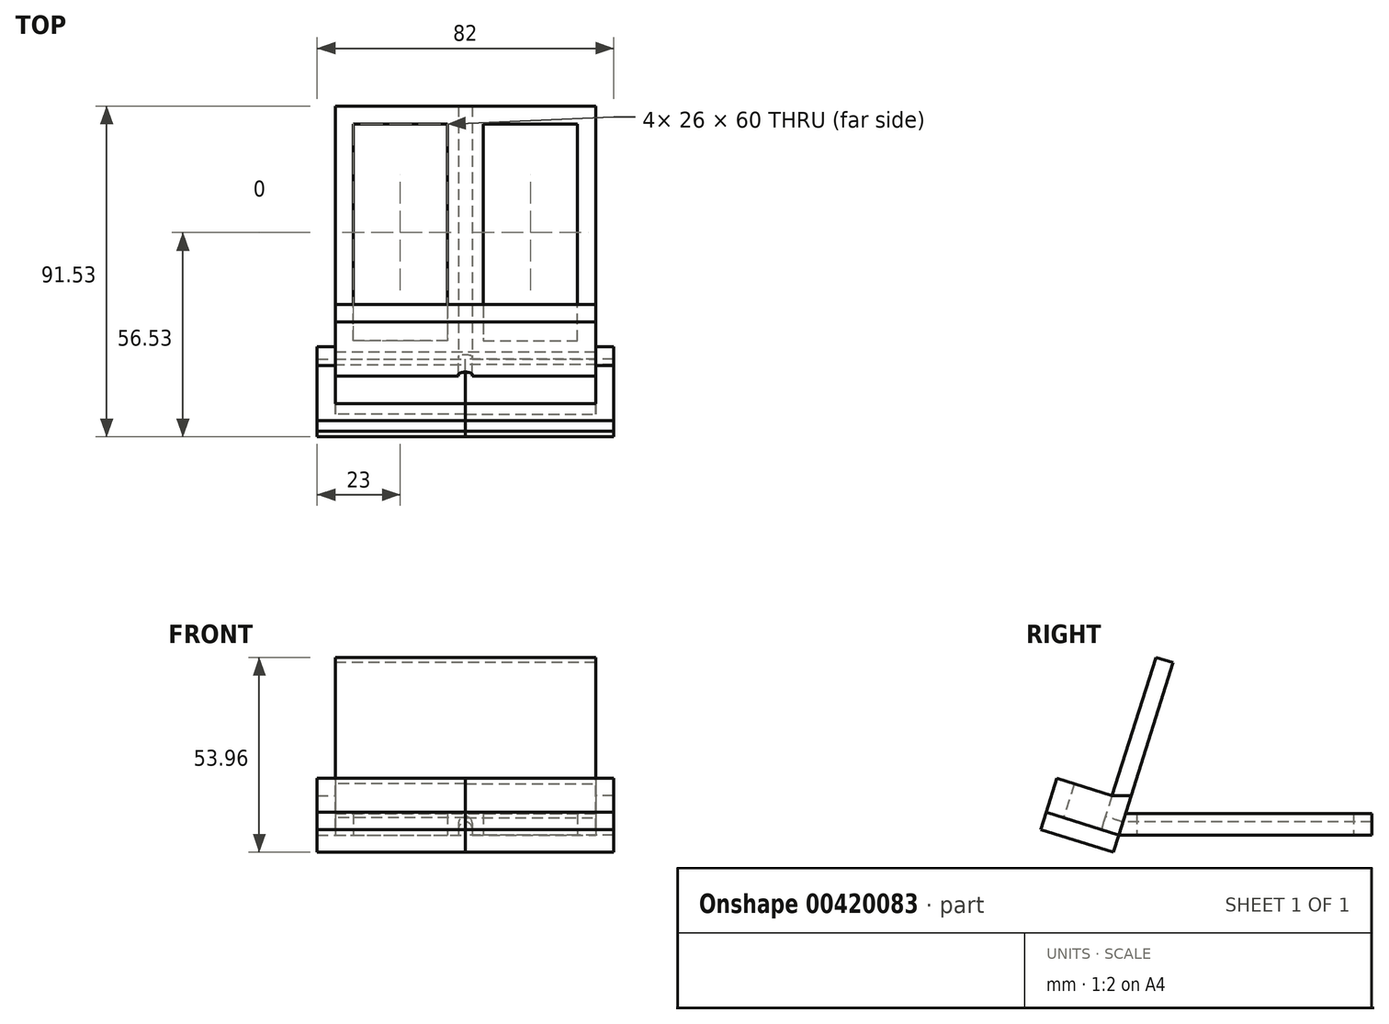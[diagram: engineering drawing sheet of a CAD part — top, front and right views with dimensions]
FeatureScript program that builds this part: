
annotation { "Feature Type Name" : "Feature", "Feature Type Description" : "" }
export const myFeature = defineFeature(function(context is Context, id is Id, definition is map)
    precondition{}
    {
        {
            var Q0;
            Q0=qCreatedBy(makeId("Top.planeOp"),FACE);
            var sketch = newSketch(context, id + "F0", { "sketchPlane" : qUnion([Q0])});
            skLineSegment(sketch, "E0", {"start": v(0, 0) * mm, "end": v(36, 0) * mm});
            skLineSegment(sketch, "E1", {"start": v(36, 0) * mm, "end": v(36, 70) * mm});
            skLineSegment(sketch, "E2", {"start": v(36, 70) * mm, "end": v(0, 70) * mm});
            skLineSegment(sketch, "E3", {"start": v(5, 65) * mm, "end": v(5, 5) * mm});
            skLineSegment(sketch, "E4", {"start": v(5, 5) * mm, "end": v(31, 5) * mm});
            skLineSegment(sketch, "E5", {"start": v(31, 5) * mm, "end": v(31, 65) * mm});
            skLineSegment(sketch, "E6", {"start": v(31, 65) * mm, "end": v(5, 65) * mm});
            skLineSegment(sketch, "E7.MirrorCS", {"start": v(-36, 70) * mm, "end": v(0, 70) * mm});
            skLineSegment(sketch, "E8.MirrorCS", {"start": v(-5, 65) * mm, "end": v(-5, 5) * mm});
            skLineSegment(sketch, "E9.MirrorCS", {"start": v(0, 0) * mm, "end": v(-36, 0) * mm});
            skLineSegment(sketch, "E10.MirrorCS", {"start": v(-36, 0) * mm, "end": v(-36, 70) * mm});
            skLineSegment(sketch, "E11.MirrorCS", {"start": v(-31, 5) * mm, "end": v(-31, 65) * mm});
            skLineSegment(sketch, "E12.MirrorCS", {"start": v(-31, 65) * mm, "end": v(-5, 65) * mm});
            skLineSegment(sketch, "E13.MirrorCS", {"start": v(-5, 5) * mm, "end": v(-31, 5) * mm});
            skSolve(sketch);
        }
        {
            var Q0;
            Q0=makeQuery(id+"F0.imprint","IMPRINT",FACE,{"disambiguationData":[TD([[makeQuery(id+"F0.imprint","IMPRINT",EDGE,{"derivedFrom":sQuery(id+"F0.wireOp",EDGE,"E0")}),1.0]])]});
            extrude(context, id + "F1", {"entities" : qUnion([Q0]), "depth" : 6 * mm});
        }
        {
            var Q0;
            Q0=makeQuery(id+"F1.opExtrude","SWEPT_FACE",FACE,{"disambiguationData":[OSD([sQuery(id+"F0.wireOp",EDGE,"E0"),sQuery(id+"F0.wireOp",EDGE,"E9.MirrorCS")])]});
            var sketch = newSketch(context, id + "F2", { "sketchPlane" : qUnion([Q0])});
            skArc(sketch, "E14", {"start": v(0, 3.65) * mm, "mid": v(-1.35, 3.1) * mm, "end": v(-1.9, 1.75) * mm});
            skLineSegment(sketch, "E15.MirrorCS", {"start": v(0, -0.15) * mm, "end": v(-1.9, -0.15) * mm});
            skLineSegment(sketch, "E16", {"start": v(-1.9, 1.75) * mm, "end": v(-1.9, -0.15) * mm});
            skPoint(sketch, "E17.orphan", {"position": v(-4.72, -0.15) * mm});
            skPoint(sketch, "E18.end.orphan", {"position": v(4.72, -0.15) * mm});
            skPoint(sketch, "E18.start.orphan", {"position": v(0, -0.15) * mm});
            skPoint(sketch, "E19.orphan", {"position": v(0, 4.82) * mm});
            skLineSegment(sketch, "E20.MirrorCS", {"start": v(1.9, 1.75) * mm, "end": v(1.9, -0.15) * mm});
            skLineSegment(sketch, "E21.MirrorCS", {"start": v(0, -0.15) * mm, "end": v(1.9, -0.15) * mm});
            skArc(sketch, "E22.MirrorCS", {"start": v(0, 3.65) * mm, "mid": v(1.35, 3.1) * mm, "end": v(1.9, 1.75) * mm});
            skSolve(sketch);
        }
        {
            var Q0;
            {var subQ5=sQuery(id+"F2.wireOp",EDGE,"E14");Q0=makeQuery(id+"F2.imprint","IMPRINT",FACE,{"disambiguationData":[TD([[makeQuery(id+"F2.imprint","IMPRINT",EDGE,{"derivedFrom":subQ5}),1.0]])]});}
            extrude(context, id + "F3", {"entities" : qUnion([Q0]), "operationType" : NewBodyOperationType.REMOVE, "oppositeDirection" : true, "depth" : 100 * mm});
        }
        {
            var Q0;
            Q0=makeQuery(id+"F1.opExtrude","SWEPT_FACE",FACE,{"disambiguationData":[OSD([sQuery(id+"F0.wireOp",EDGE,"E1")])]});
            var sketch = newSketch(context, id + "F4", { "sketchPlane" : qUnion([Q0])});
            skLineSegment(sketch, "E23", {"start": v(0, 0) * mm, "end": v(1.9, 6) * mm});
            skLineSegment(sketch, "E24", {"start": v(1.9, 6) * mm, "end": v(0, 6) * mm});
            skLineSegment(sketch, "E25", {"start": v(0, 6) * mm, "end": v(0, 0) * mm});
            skSolve(sketch);
        }
        {
            var Q0;
            Q0=makeQuery(id+"F4.imprint","IMPRINT",FACE,{"disambiguationData":[TD([[makeQuery(id+"F4.imprint","IMPRINT",EDGE,{"derivedFrom":sQuery(id+"F4.wireOp",EDGE,"E23")}),1.0]])]});
            extrude(context, id + "F5", {"entities" : qUnion([Q0]), "operationType" : NewBodyOperationType.REMOVE, "oppositeDirection" : true, "depth" : 75 * mm});
        }
        {
            var Q0;
            Q0=makeQuery(id+"F5.boolean.opBoolean","COPY",FACE,{"derivedFrom":makeQuery(id+"F5.opExtrude","SWEPT_FACE",FACE,{"disambiguationData":[OSD([sQuery(id+"F4.wireOp",EDGE,"E23")])]})});
            var sketch = newSketch(context, id + "F6", { "sketchPlane" : qUnion([Q0])});
            skLineSegment(sketch, "E26", {"start": v(-36, 0) * mm, "end": v(-36, 50) * mm});
            skLineSegment(sketch, "E27", {"start": v(-36, 50) * mm, "end": v(36, 50) * mm});
            skLineSegment(sketch, "E28", {"start": v(36, 50) * mm, "end": v(36, 0) * mm});
            skSolve(sketch);
        }
        {
            var Q0;
            {var subQ2=sQuery(id+"F6.wireOp",EDGE,"E27");Q0=makeQuery(id+"F6.imprint","IMPRINT",FACE,{"disambiguationData":[TD([[makeQuery(id+"F6.imprint","IMPRINT",EDGE,{"derivedFrom":subQ2}),-1.0]])]});}
            var Q1;
            {var subQ0=sQuery(id+"F4.wireOp",EDGE,"E23");var subQ13=makeQuery(id+"F3.opExtrude","SWEPT_FACE",FACE,{"disambiguationData":[OSD([sQuery(id+"F2.wireOp",EDGE,"E16")])]});var subQ16=makeQuery(id+"F5.opExtrude","SWEPT_FACE",FACE,{"disambiguationData":[OSD([subQ0])]});Q1=makeQuery(id+"F6.imprint","IMPRINT",FACE,{"disambiguationData":[TD([[makeQuery(id+"F6.imprint","IMPRINT",EDGE,{"derivedFrom":makeQuery(id+"F5.boolean.opBoolean","INTERSECT",EDGE,{"derivedFrom":[makeQuery(id+"F3.boolean.opBoolean","COPY",FACE,{"derivedFrom":subQ13}),subQ16]})}),-1.0]])]});}
            extrude(context, id + "F7", {"entities" : qUnion([Q0, Q1]), "operationType" : NewBodyOperationType.ADD, "depth" : 5 * mm});
        }
        {
            var Q0;
            Q0=makeQuery(id+"F7.boolean.opBoolean","MERGE",FACE,{"derivedFrom":[makeQuery(id+"F1.opExtrude","SWEPT_FACE",FACE,{"disambiguationData":[OSD([sQuery(id+"F0.wireOp",EDGE,"E1")])]}),makeQuery(id+"F7.opExtrude","SWEPT_FACE",FACE,{"disambiguationData":[OSD([sQuery(id+"F6.wireOp",EDGE,"E28")])]})]});
            var sketch = newSketch(context, id + "F8", { "sketchPlane" : qUnion([Q0])});
            skLineSegment(sketch, "E29", {"start": v(-1.8, 10.89) * mm, "end": v(3.44, 10.89) * mm});
            skLineSegment(sketch, "E30", {"start": v(3.44, 10.89) * mm, "end": v(0, 0) * mm});
            skLineSegment(sketch, "E31", {"start": v(0, 0) * mm, "end": v(-4.77, 1.5) * mm});
            skLineSegment(sketch, "E32", {"start": v(-4.77, 1.5) * mm, "end": v(-1.8, 10.89) * mm});
            skSolve(sketch);
        }
        {
            var Q0;
            {var subQ4=sQuery(id+"F8.wireOp",EDGE,"E29");Q0=makeQuery(id+"F8.imprint","IMPRINT",FACE,{"disambiguationData":[TD([[makeQuery(id+"F8.imprint","IMPRINT",EDGE,{"derivedFrom":subQ4}),-1.0]])]});}
            extrude(context, id + "F9", {"entities" : qUnion([Q0]), "operationType" : NewBodyOperationType.ADD, "depth" : 5 * mm});
        }
        {
            var Q0;
            Q0=makeQuery(id+"F9.boolean.opBoolean","MERGE",FACE,{"derivedFrom":[makeQuery(id+"F7.opExtrude","CAP_FACE",FACE,{"disambiguationData":[OSD([sQuery(id+"F0.wireOp",EDGE,"E0"),sQuery(id+"F0.wireOp",EDGE,"E1"),sQuery(id+"F0.wireOp",EDGE,"E9.MirrorCS"),sQuery(id+"F2.wireOp",EDGE,"E14"),sQuery(id+"F2.wireOp",EDGE,"E16"),sQuery(id+"F2.wireOp",EDGE,"E20.MirrorCS"),sQuery(id+"F2.wireOp",EDGE,"E22.MirrorCS"),sQuery(id+"F4.wireOp",EDGE,"E23"),sQuery(id+"F4.wireOp",EDGE,"E25"),sQuery(id+"F6.wireOp",EDGE,"E26"),sQuery(id+"F6.wireOp",EDGE,"E27"),sQuery(id+"F6.wireOp",EDGE,"E28")])],"isStart":false}),makeQuery(id+"F9.opExtrude","SWEPT_FACE",FACE,{"disambiguationData":[OSD([sQuery(id+"F8.wireOp",EDGE,"E32")])]})]});
            var sketch = newSketch(context, id + "F10", { "sketchPlane" : qUnion([Q0])});
            skLineSegment(sketch, "E33", {"start": v(36, 9.84) * mm, "end": v(36, 0) * mm});
            skSolve(sketch);
        }
        {
            var Q0;
            {var subQ0=sQuery(id+"F10.wireOp",EDGE,"E33");Q0=makeQuery(id+"F10.imprint","IMPRINT",FACE,{"disambiguationData":[TD([[makeQuery(id+"F10.imprint","IMPRINT",EDGE,{"derivedFrom":subQ0}),1.0]])]});}
            extrude(context, id + "F11", {"entities" : qUnion([Q0]), "operationType" : NewBodyOperationType.ADD, "depth" : 16 * mm});
        }
        {
            var Q0;
            Q0=makeQuery(id+"F11.opExtrude","SWEPT_FACE",FACE,{"disambiguationData":[OSD([sQuery(id+"F10.wireOp",EDGE,"E33")])]});
            var sketch = newSketch(context, id + "F12", { "sketchPlane" : qUnion([Q0])});
            skLineSegment(sketch, "E34", {"start": v(17.07, 15.7) * mm, "end": v(12.3, 14.2) * mm});
            skPoint(sketch, "E35.endSnap0", {"position": v(12.4, 3.91) * mm});
            skPoint(sketch, "E35.end.orphan", {"position": v(15.54, 3.91) * mm});
            skLineSegment(sketch, "E36", {"start": v(12.3, 14.2) * mm, "end": v(15.26, 4.82) * mm});
            skSolve(sketch);
        }
        {
            var Q0;
            Q0=makeQuery(id+"F12.imprint","IMPRINT",FACE,{"disambiguationData":[TD([[makeQuery(id+"F12.imprint","IMPRINT",EDGE,{"derivedFrom":sQuery(id+"F12.wireOp",EDGE,"E34")}),1.0]])]});
            extrude(context, id + "F13", {"entities" : qUnion([Q0]), "operationType" : NewBodyOperationType.ADD, "depth" : 36 * mm});
        }
        {
            var Q0;
            Q0=makeQuery(id+"F1.opExtrude","SWEPT_BODY",BODY,{"disambiguationData":[OSD([sQuery(id+"F0.wireOp",EDGE,"E0"),sQuery(id+"F0.wireOp",EDGE,"E1"),sQuery(id+"F0.wireOp",EDGE,"E2"),sQuery(id+"F0.wireOp",EDGE,"E3"),sQuery(id+"F0.wireOp",EDGE,"E4"),sQuery(id+"F0.wireOp",EDGE,"E5"),sQuery(id+"F0.wireOp",EDGE,"E6"),sQuery(id+"F0.wireOp",EDGE,"E7.MirrorCS"),sQuery(id+"F0.wireOp",EDGE,"E8.MirrorCS"),sQuery(id+"F0.wireOp",EDGE,"E9.MirrorCS"),sQuery(id+"F0.wireOp",EDGE,"E10.MirrorCS"),sQuery(id+"F0.wireOp",EDGE,"E11.MirrorCS"),sQuery(id+"F0.wireOp",EDGE,"E12.MirrorCS"),sQuery(id+"F0.wireOp",EDGE,"E13.MirrorCS")])]});
            var Q1;
            Q1=qCreatedBy(makeId("Right.planeOp"),FACE);
            mirror(context, id + "F14", {"entities" : qUnion([Q0]), "mirrorPlane" : qUnion([Q1])});
        }
        {
            var Q0;
            {var subQ0=sQuery(id+"F8.wireOp",EDGE,"E32");var subQ1=sQuery(id+"F8.wireOp",EDGE,"E31");var subQ2=sQuery(id+"F4.wireOp",EDGE,"E25");var subQ3=sQuery(id+"F4.wireOp",EDGE,"E23");var subQ4=sQuery(id+"F0.wireOp",EDGE,"E9.MirrorCS");var subQ5=sQuery(id+"F0.wireOp",EDGE,"E1");var subQ6=sQuery(id+"F0.wireOp",EDGE,"E0");Q0=makeQuery(id+"F13.boolean.opBoolean","MERGE",FACE,{"derivedFrom":[makeQuery(id+"F11.boolean.opBoolean","MERGE",FACE,{"derivedFrom":[makeQuery(id+"F9.boolean.opBoolean","MERGE",FACE,{"derivedFrom":[makeQuery(id+"F7.opExtrude","SWEPT_FACE",FACE,{"disambiguationData":[OSD([subQ6,subQ5,subQ4,subQ3,subQ2]),TDD([makeQuery(id+"F6.imprint","IMPRINT",EDGE,{"derivedFrom":makeQuery(id+"F5.boolean.opBoolean","MERGE",EDGE,{"derivedFrom":[makeQuery(id+"F3.boolean.opBoolean","SPLIT",EDGE,{"disambiguationData":[TD([makeQuery(id+"F1.opExtrude","SWEPT_FACE",FACE,{"disambiguationData":[OSD([subQ5])]})])],"derivedFrom":makeQuery(id+"F1.opExtrude","CAP_EDGE",EDGE,{"disambiguationData":[OSD([subQ6,subQ4])],"isStart":true})}),makeQuery(id+"F5.opExtrude","SWEPT_EDGE",EDGE,{"disambiguationData":[OSD([subQ5,subQ3,subQ2])]})]})})])]}),makeQuery(id+"F9.opExtrude","SWEPT_FACE",FACE,{"disambiguationData":[OSD([subQ1])]})]}),makeQuery(id+"F11.opExtrude","SWEPT_FACE",FACE,{"disambiguationData":[OSD([subQ6,subQ5,subQ4,subQ3,subQ2,subQ1,subQ0])]})]}),makeQuery(id+"F13.opExtrude","SWEPT_FACE",FACE,{"disambiguationData":[OSD([subQ6,subQ5,subQ4,subQ3,subQ2,subQ1,subQ0,sQuery(id+"F10.wireOp",EDGE,"E33")])]})]});}
            var sketch = newSketch(context, id + "F15", { "sketchPlane" : qUnion([Q0])});
            skLineSegment(sketch, "E37", {"start": v(0, 21) * mm, "end": v(0, 0) * mm});
            skLineSegment(sketch, "E38", {"start": v(0, 0) * mm, "end": v(3.5, 0) * mm});
            skSolve(sketch);
        }
        {
            var Q0;
            {var subQ0=sQuery(id+"F8.wireOp",EDGE,"E31");var subQ1=sQuery(id+"F0.wireOp",EDGE,"E1");var subQ2=makeQuery(id+"F9.opExtrude","SWEPT_EDGE",EDGE,{"disambiguationData":[OSD([subQ1,sQuery(id+"F8.wireOp",EDGE,"E30"),subQ0])]});Q0=makeQuery(id+"F15.imprint","IMPRINT",FACE,{"disambiguationData":[TD([[makeQuery(id+"F15.imprint","IMPRINT",EDGE,{"derivedFrom":subQ2}),-1.0]])]});}
            var Q1;
            {var subQ0=sQuery(id+"F4.wireOp",EDGE,"E25");var subQ1=sQuery(id+"F4.wireOp",EDGE,"E23");var subQ2=sQuery(id+"F2.wireOp",EDGE,"E20.MirrorCS");var subQ3=sQuery(id+"F0.wireOp",EDGE,"E9.MirrorCS");var subQ4=sQuery(id+"F0.wireOp",EDGE,"E1");var subQ5=sQuery(id+"F0.wireOp",EDGE,"E0");var subQ6=makeQuery(id+"F7.opExtrude","SWEPT_EDGE",EDGE,{"disambiguationData":[OSD([subQ5,subQ4,subQ3,subQ2,subQ1,subQ0])]});Q1=makeQuery(id+"F15.imprint","IMPRINT",FACE,{"disambiguationData":[TD([[makeQuery(id+"F15.imprint","IMPRINT",EDGE,{"derivedFrom":subQ6}),-1.0]])]});}
            extrude(context, id + "F16", {"entities" : qUnion([Q0, Q1]), "depth" : 5 * mm});
        }
        {
            var Q0;
            Q0=makeQuery(id+"F16.opExtrude","SWEPT_BODY",BODY,{"disambiguationData":[OSD([sQuery(id+"F0.wireOp",EDGE,"E0"),sQuery(id+"F0.wireOp",EDGE,"E1"),sQuery(id+"F0.wireOp",EDGE,"E9.MirrorCS"),sQuery(id+"F4.wireOp",EDGE,"E23"),sQuery(id+"F4.wireOp",EDGE,"E25"),sQuery(id+"F8.wireOp",EDGE,"E30"),sQuery(id+"F8.wireOp",EDGE,"E31"),sQuery(id+"F8.wireOp",EDGE,"E32"),sQuery(id+"F10.wireOp",EDGE,"E33"),sQuery(id+"F15.wireOp",EDGE,"E37"),sQuery(id+"F15.wireOp",EDGE,"E38")])]});
            var Q1;
            Q1=qCreatedBy(makeId("Right.planeOp"),FACE);
            mirror(context, id + "F17", {"entities" : qUnion([Q0]), "mirrorPlane" : qUnion([Q1])});
        }
    });
